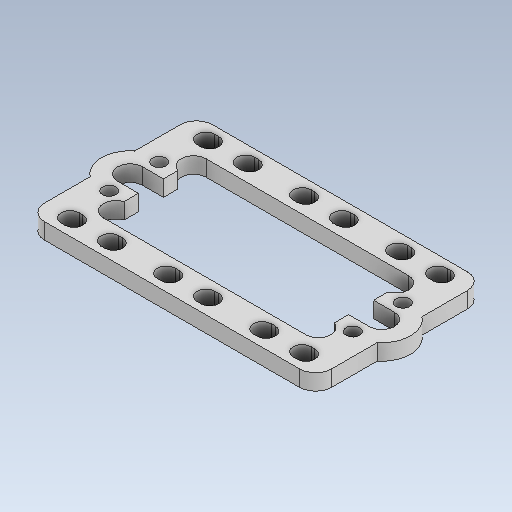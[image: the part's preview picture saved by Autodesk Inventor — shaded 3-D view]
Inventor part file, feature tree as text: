
AUTODESK INVENTOR PART (.ipt)
format: ipt  version: 2020.1 (Build 241239000, 239)  size: 181,760 bytes
history: native  units: in
note: dims shown in document units (in); Inventor stores cm internally (conversion verified against a paired STEP export)
features: mirror x1
ambient origin geometry x8: Origin, YZ Plane, XZ Plane, XY Plane, X Axis, Y Axis, Z Axis, Center Point
bodies: Solid1 (feature_tree)
feature tree (1):
  mirror  "Mirror2"
